FCSTD DOCUMENT  (FreeCAD 0.19R24276 (Git))
Label: Bearing_fix_22x8x7_V1
License: All rights reserved
LicenseURL: http://en.wikipedia.org/wiki/All_rights_reserved
objects: Sketcher::SketchObject×1, PartDesign::Body×1
note: 2 computed .brp shape members not serialized (recipe doc carries the construction recipe); baked Part::Feature solids carry a one-line shape summary decoded from their .brp

FEATURE [Sketcher::SketchObject] Sketch
  FullyConstrained = true
  MapMode = 5
  Support = -> [XY_Plane]
  sketch-geometry (14):
    g0: Circle CenterX=8.3 CenterY=44.5 CenterZ=0 NormalX=0 NormalY=0 NormalZ=1 AngleXU=0 Radius=2.5
    g1: Circle CenterX=26.7 CenterY=44.5 CenterZ=0 NormalX=0 NormalY=0 NormalZ=1 AngleXU=0 Radius=2.5
    g2: Circle CenterX=8.3 CenterY=23.5 CenterZ=0 NormalX=0 NormalY=0 NormalZ=1 AngleXU=0 Radius=2.5
    g3: Circle CenterX=26.7 CenterY=23.5 CenterZ=0 NormalX=0 NormalY=0 NormalZ=1 AngleXU=0 Radius=2.5
    g4: LineSegment StartX=0 StartY=50 StartZ=0 EndX=35 EndY=50 EndZ=0
    g5: LineSegment StartX=35 StartY=50 StartZ=0 EndX=35 EndY=0 EndZ=0
    g6: LineSegment StartX=35 StartY=0 StartZ=0 EndX=0 EndY=0 EndZ=0
    g7: LineSegment StartX=0 StartY=0 StartZ=0 EndX=0 EndY=50 EndZ=0
    g8: LineSegment StartX=8.3 StartY=44.5 StartZ=0 EndX=26.7 EndY=23.5 EndZ=0
    g9: LineSegment StartX=8.3 StartY=23.5 StartZ=0 EndX=26.7 EndY=44.5 EndZ=0
    g10: GeomPoint X=17.5 Y=34 Z=0
    g11: GeomPoint X=17.5 Y=34 Z=0
    g12: Circle CenterX=17.5 CenterY=34 CenterZ=0 NormalX=0 NormalY=0 NormalZ=1 AngleXU=0 Radius=5.5
    g13: LineSegment StartX=17.5 StartY=34 StartZ=0 EndX=17.5 EndY=50 EndZ=0
  constraints (34):
    c: Diameter(g0) = 5
    c: Equal(g0,g1)
    c: Equal(g0,g3)
    c: Equal(g0,g2)
    c: Horizontal(g0,g1)
    c: Horizontal(g2,g3)
    c: DistanceX(g2,g3) = 18.4
    c: Coincident(g4,g5)
    c: Coincident(g5,g6)
    c: Coincident(g6,g7)
    c: Coincident(g7,g4)
    c: Horizontal(g4)
    c: Horizontal(g6)
    c: Vertical(g5)
    c: Vertical(g7)
    c: DistanceX(g4,g4) = 35
    c: DistanceY(g5,g5) = 50
    c: Coincident(g6,g-1)
    c: Vertical(g2,g0)
    c: Vertical(g1,g3)
    c: DistanceY(g3,g1) = 21
    c: Coincident(g8,g0)
    c: Coincident(g8,g3)
    c: Coincident(g9,g2)
    c: Coincident(g9,g1)
    c: PointOnObject(g10,g8)
    c: PointOnObject(g11,g9)
    c: Coincident(g10,g11)
    c: Coincident(g12,g10)
    c: Diameter(g12) = 11
    c: Coincident(g13,g10)
    c: Vertical(g13)
    c: Symmetric(g4,g4,g13)
    c: DistanceY(g1,g4) = 5.5
FEATURE [PartDesign::Body] Body
  Group = -> [Sketch]
  Origin = -> Origin
